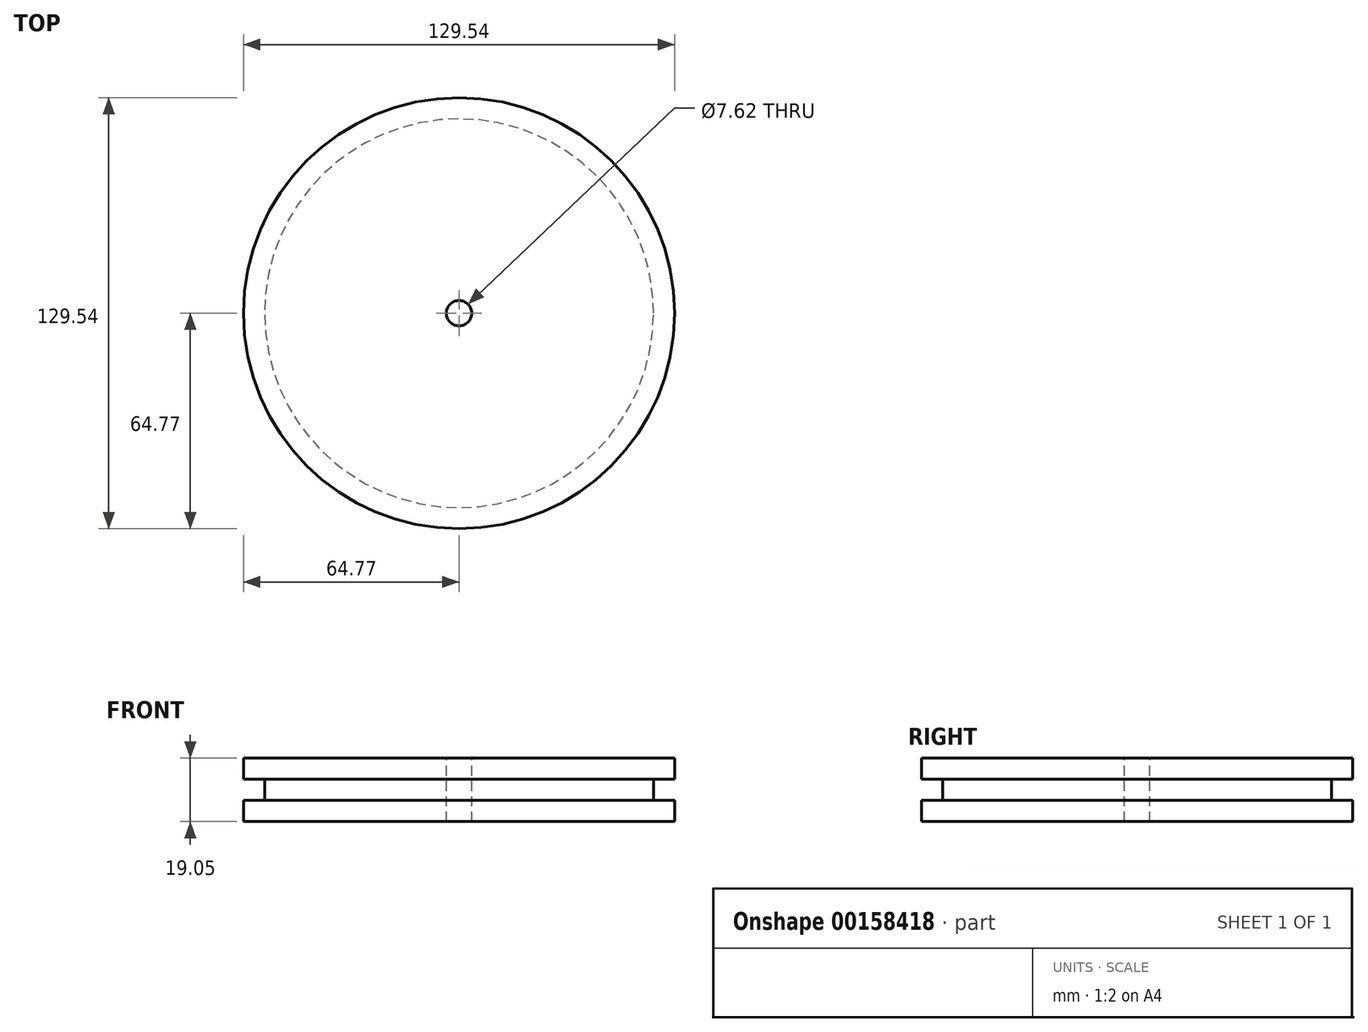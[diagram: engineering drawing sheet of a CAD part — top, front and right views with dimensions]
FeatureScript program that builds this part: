
annotation { "Feature Type Name" : "Feature", "Feature Type Description" : "" }
export const myFeature = defineFeature(function(context is Context, id is Id, definition is map)
    precondition{}
    {
        {
            var Q0;
            Q0=qCreatedBy(makeId("Top.planeOp"),FACE);
            var sketch = newSketch(context, id + "F0", { "sketchPlane" : qUnion([Q0])});
            skCircle(sketch, "E0", {"center": v(0, 0) * mm, "radius": 58.42 * mm});
            skSolve(sketch);
        }
        {
            var Q0;
            Q0=makeQuery(id+"F0.imprint","IMPRINT",FACE,{"disambiguationData":[TD([[makeQuery(id+"F0.imprint","IMPRINT",EDGE,{"derivedFrom":sQuery(id+"F0.wireOp",EDGE,"E0")}),1.0]])]});
            extrude(context, id + "F1", {"entities" : qUnion([Q0]), "depth" : 6.35 * mm});
        }
        {
            var Q0;
            Q0=makeQuery(id+"F1.opExtrude","CAP_FACE",FACE,{"disambiguationData":[OSD([sQuery(id+"F0.wireOp",EDGE,"E0")])],"isStart":false});
            var sketch = newSketch(context, id + "F2", { "sketchPlane" : qUnion([Q0])});
            skCircle(sketch, "E1", {"center": v(0, 0) * mm, "radius": 3.81 * mm});
            skSolve(sketch);
        }
        {
            var Q0;
            Q0=makeQuery(id+"F2.imprint","IMPRINT",FACE,{"disambiguationData":[TD([[makeQuery(id+"F2.imprint","IMPRINT",EDGE,{"derivedFrom":sQuery(id+"F2.wireOp",EDGE,"E1")}),1.0]])]});
            extrude(context, id + "F3", {"entities" : qUnion([Q0]), "operationType" : NewBodyOperationType.REMOVE, "oppositeDirection" : true, "depth" : 25.4 * mm});
        }
        {
            var Q0;
            Q0=makeQuery(id+"F1.opExtrude","CAP_FACE",FACE,{"disambiguationData":[OSD([sQuery(id+"F0.wireOp",EDGE,"E0")])],"isStart":false});
            var sketch = newSketch(context, id + "F4", { "sketchPlane" : qUnion([Q0])});
            skCircle(sketch, "E2.0", {"center": v(0, 0) * mm, "radius": 64.77 * mm});
            skSolve(sketch);
        }
        {
            var Q0;
            Q0=makeQuery(id+"F4.imprint","IMPRINT",FACE,{"disambiguationData":[TD([[makeQuery(id+"F4.imprint","IMPRINT",EDGE,{"derivedFrom":makeQuery(id+"F1.opExtrude","CAP_EDGE",EDGE,{"disambiguationData":[OSD([sQuery(id+"F0.wireOp",EDGE,"E0")])],"isStart":false})}),1.0]])]});
            var Q1;
            Q1=makeQuery(id+"F4.imprint","IMPRINT",FACE,{"disambiguationData":[TD([[makeQuery(id+"F4.imprint","IMPRINT",EDGE,{"derivedFrom":sQuery(id+"F4.wireOp",EDGE,"E2.0")}),1.0]])]});
            extrude(context, id + "F5", {"entities" : qUnion([Q0, Q1]), "operationType" : NewBodyOperationType.ADD, "depth" : 6.35 * mm});
        }
        {
            var Q0;
            Q0=makeQuery(id+"F1.opExtrude","CAP_FACE",FACE,{"disambiguationData":[OSD([sQuery(id+"F0.wireOp",EDGE,"E0")])],"isStart":true});
            var sketch = newSketch(context, id + "F6", { "sketchPlane" : qUnion([Q0])});
            skCircle(sketch, "E3.0", {"center": v(0, 0) * mm, "radius": 64.77 * mm});
            skSolve(sketch);
        }
        {
            var Q0;
            Q0=makeQuery(id+"F6.imprint","IMPRINT",FACE,{"disambiguationData":[TD([[makeQuery(id+"F6.imprint","IMPRINT",EDGE,{"derivedFrom":sQuery(id+"F6.wireOp",EDGE,"E3.0")}),1.0]])]});
            var Q1;
            {var subQ0=sQuery(id+"F0.wireOp",EDGE,"E0");Q1=makeQuery(id+"F6.imprint","IMPRINT",FACE,{"disambiguationData":[TD([[makeQuery(id+"F6.imprint","IMPRINT",EDGE,{"derivedFrom":makeQuery(id+"F1.opExtrude","CAP_EDGE",EDGE,{"disambiguationData":[OSD([subQ0])],"isStart":true})}),-1.0]])]});}
            extrude(context, id + "F7", {"entities" : qUnion([Q0, Q1]), "operationType" : NewBodyOperationType.ADD, "depth" : 6.35 * mm});
        }
    });
